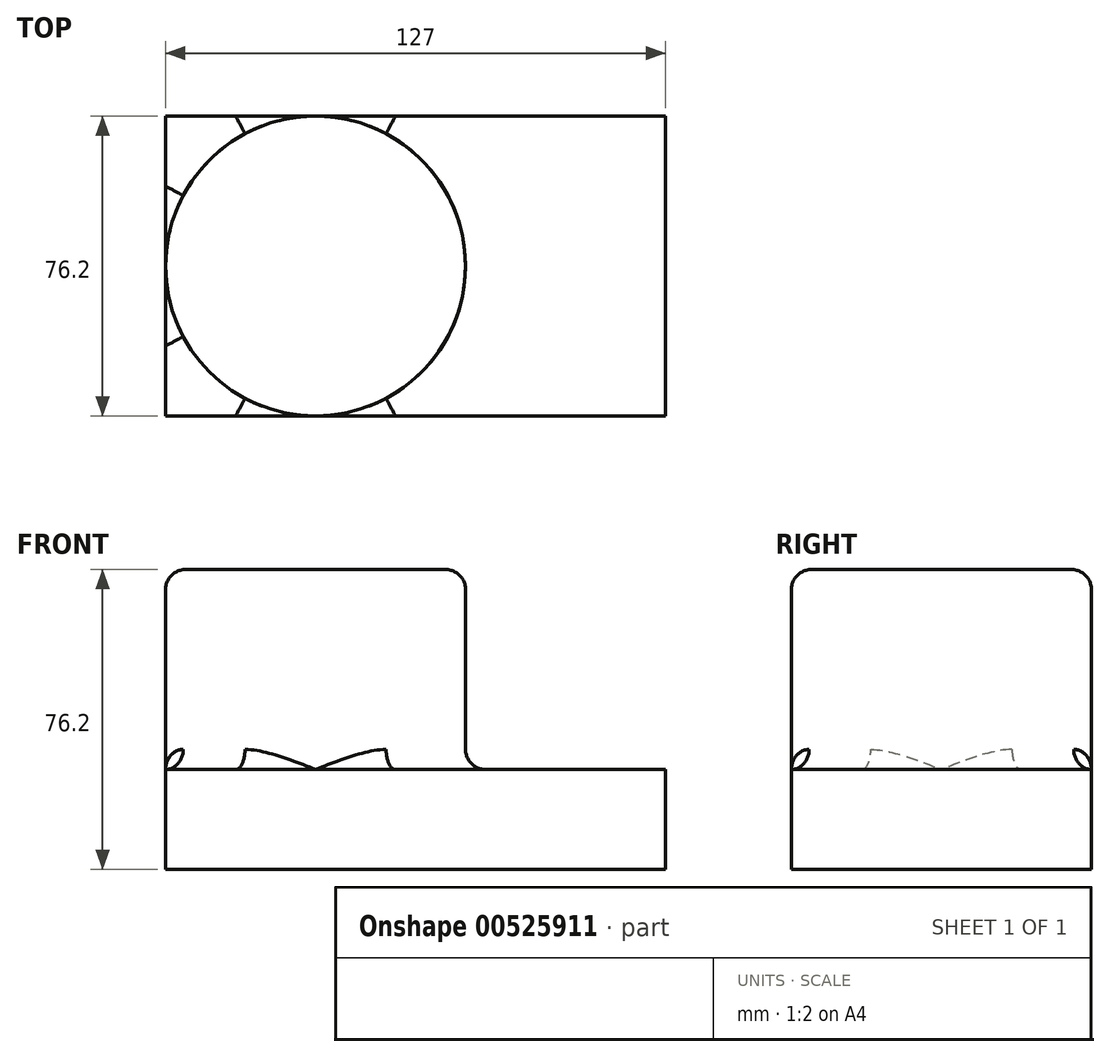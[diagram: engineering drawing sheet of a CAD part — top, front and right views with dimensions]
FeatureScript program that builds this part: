
annotation { "Feature Type Name" : "Feature", "Feature Type Description" : "" }
export const myFeature = defineFeature(function(context is Context, id is Id, definition is map)
    precondition{}
    {
        {
            var Q0;
            Q0=qCreatedBy(makeId("Top.planeOp"),FACE);
            var sketch = newSketch(context, id + "F0", { "sketchPlane" : qUnion([Q0])});
            skLineSegment(sketch, "E0.bottom", {"start": v(0, 0) * mm, "end": v(127, 0) * mm});
            skLineSegment(sketch, "E0.top", {"start": v(0, 76.2) * mm, "end": v(127, 76.2) * mm});
            skLineSegment(sketch, "E0.left", {"start": v(0, 0) * mm, "end": v(0, 76.2) * mm});
            skLineSegment(sketch, "E0.right", {"start": v(127, 0) * mm, "end": v(127, 76.2) * mm});
            skPoint(sketch, "E1.middle", {"position": v(0, 0) * mm});
            skCircle(sketch, "E2", {"center": v(38.1, 38.1) * mm, "radius": 38.1 * mm});
            skPoint(sketch, "E2.first.point", {"position": v(38.1, 76.2) * mm});
            skPoint(sketch, "E2.second.point", {"position": v(0, 38.1) * mm});
            skPoint(sketch, "E2.third.point", {"position": v(38.1, 0) * mm});
            skPoint(sketch, "E3", {"position": v(106.36, 42.18) * mm});
            skSolve(sketch);
        }
        {
            var Q0;
            {var subQ0=sQuery(id+"F0.wireOp",EDGE,"E2");var subQ1=makeQuery(id+"F0.imprint","INTERSECT",VERTEX,{"derivedFrom":[sQuery(id+"F0.wireOp",EDGE,"E0.top"),subQ0]});Q0=makeQuery(id+"F0.imprint","IMPRINT",FACE,{"disambiguationData":[TD([[makeQuery(id+"F0.imprint","IMPRINT",EDGE,{"disambiguationData":[TD([[subQ1,-1.0]])],"derivedFrom":subQ0}),1.0]])]});}
            extrude(context, id + "F1", {"entities" : qUnion([Q0]), "depth" : 50.8 * mm, "offsetDistance" : 25.4 * mm, "hasDraft" : true, "draftAngle" : 0 * degree});
        }
        {
            var Q0;
            Q0=qSketchRegion(id+"F0",true);
            extrude(context, id + "F2", {"entities" : qUnion([Q0]), "operationType" : NewBodyOperationType.ADD, "oppositeDirection" : true, "depth" : 25.4 * mm, "offsetDistance" : 25.4 * mm});
        }
        {
            var Q0;
            Q0=makeQuery(id+"F1.opExtrude","CAP_EDGE",EDGE,{"disambiguationData":[OSD([sQuery(id+"F0.wireOp",EDGE,"E2")])],"isStart":false});
            var Q1;
            {var subQ0=sQuery(id+"F0.wireOp",EDGE,"E2");var subQ1=sQuery(id+"F0.wireOp",EDGE,"E0.bottom");var subQ2=sQuery(id+"F0.wireOp",EDGE,"E0.top");Q1=makeQuery(id+"F2.boolean.opBoolean","SPLIT",EDGE,{"disambiguationData":[TD([makeQuery(id+"F1.opExtrude","SWEPT_FACE",FACE,{"disambiguationData":[OSD([subQ0])]}),makeQuery(id+"F2.opExtrude","SWEPT_FACE",FACE,{"disambiguationData":[OSD([subQ1])]}),makeQuery(id+"F2.opExtrude","CAP_FACE",FACE,{"disambiguationData":[OSD([subQ1,subQ2,sQuery(id+"F0.wireOp",EDGE,"E0.left"),sQuery(id+"F0.wireOp",EDGE,"E0.right")])],"isStart":true}),makeQuery(id+"F2.opExtrude","SWEPT_FACE",FACE,{"disambiguationData":[OSD([subQ2])]})])],"derivedFrom":makeQuery(id+"F1.opExtrude","CAP_EDGE",EDGE,{"disambiguationData":[OSD([subQ0])],"isStart":true})});}
            fillet(context, id + "F3", {"entities" : qUnion([Q0, Q1]), "radius" : 5.08 * mm, "tangentPropagation" : true, "allowEdgeOverflow" : false});
        }
    });
